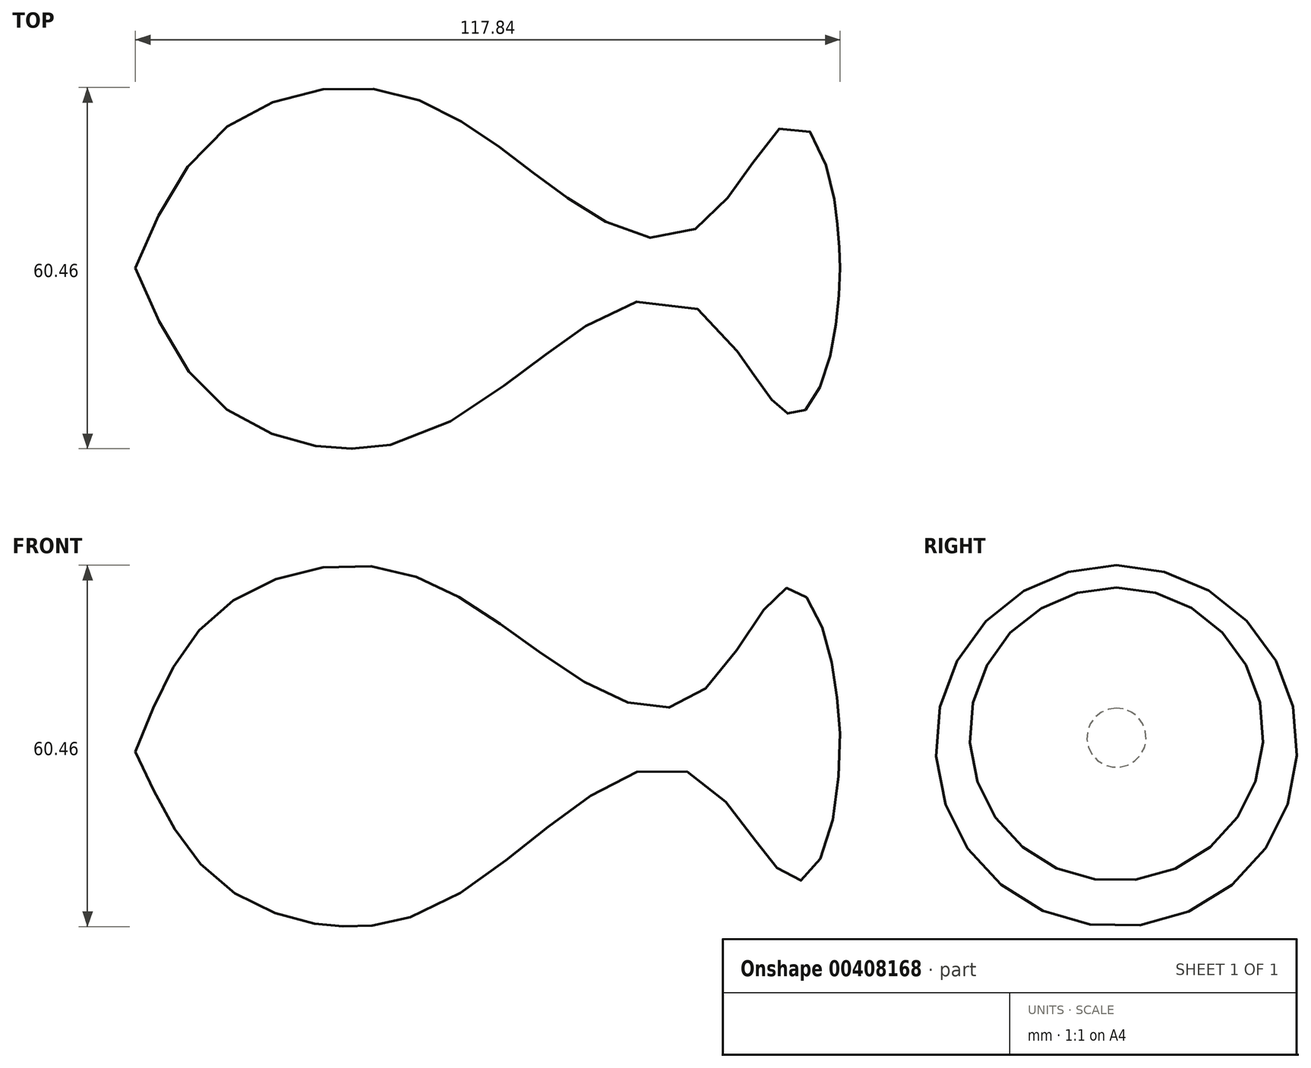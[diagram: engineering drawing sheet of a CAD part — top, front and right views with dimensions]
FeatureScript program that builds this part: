
annotation { "Feature Type Name" : "Feature", "Feature Type Description" : "" }
export const myFeature = defineFeature(function(context is Context, id is Id, definition is map)
    precondition{}
    {
        {
            var Q0;
            Q0=qCreatedBy(makeId("Front.planeOp"),FACE);
            var sketch = newSketch(context, id + "F0", { "sketchPlane" : qUnion([Q0])});
            skFitSpline(sketch, "E0", {"points": [v(-50.83, 13.9) * mm, v(-36.93, 37.34) * mm, v(-9.13, 44.6) * mm, v(18.05, 29.67) * mm, v(42.11, 22.61) * mm, v(58.09, 41.28) * mm, v(64.31, 33.82) * mm, v(67, 17.01) * mm], "startDerivative": vector(65.66, 168.47) * mm, "endDerivative": vector(10.11, -137.11) * mm});
            skLineSegment(sketch, "E1", {"start": v(67, 17.01) * mm, "end": v(-50.83, 13.9) * mm, "construction": true});
            skSolve(sketch);
        }
        {
            var Q0;
            Q0=sQuery(id+"F0.wireOp",EDGE,"E0");
            var Q1;
            Q1=sQuery(id+"F0.wireOp",EDGE,"E1");
            revolve(context, id + "F1", {"bodyType" : ToolBodyType.SURFACE, "surfaceEntities" : qUnion([Q0]), "axis" : qUnion([Q1]), "revolveType" : RevolveType.FULL});
        }
    });
